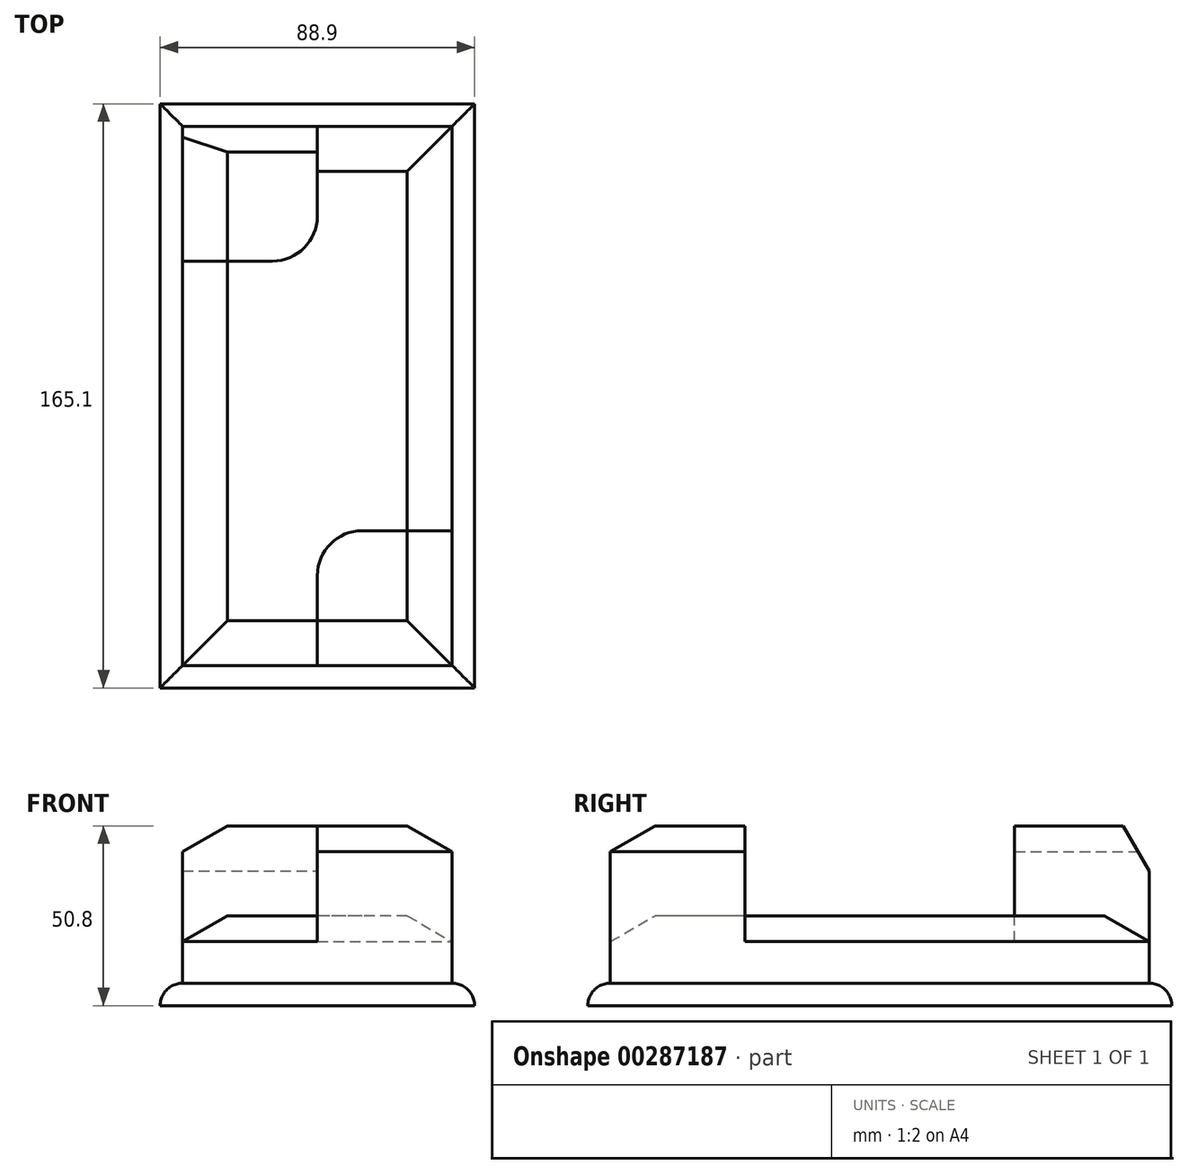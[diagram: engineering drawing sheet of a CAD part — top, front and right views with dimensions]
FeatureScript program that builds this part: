
annotation { "Feature Type Name" : "Feature", "Feature Type Description" : "" }
export const myFeature = defineFeature(function(context is Context, id is Id, definition is map)
    precondition{}
    {
        {
            var Q0;
            Q0=qCreatedBy(makeId("Top.planeOp"),FACE);
            var sketch = newSketch(context, id + "F0", { "sketchPlane" : qUnion([Q0])});
            skLineSegment(sketch, "E0.bottom", {"start": v(-49.01, 97.54) * mm, "end": v(27.19, 97.54) * mm});
            skLineSegment(sketch, "E0.top", {"start": v(-49.01, -54.86) * mm, "end": v(27.19, -54.86) * mm});
            skLineSegment(sketch, "E0.left", {"start": v(-49.01, 97.54) * mm, "end": v(-49.01, -54.86) * mm});
            skLineSegment(sketch, "E0.right", {"start": v(27.19, 97.54) * mm, "end": v(27.19, -54.86) * mm});
            skLineSegment(sketch, "E1.0", {"start": v(-55.36, 103.89) * mm, "end": v(-55.36, -61.21) * mm});
            skLineSegment(sketch, "E1.1", {"start": v(-55.36, 103.89) * mm, "end": v(33.54, 103.89) * mm});
            skLineSegment(sketch, "E1.2", {"start": v(33.54, 103.89) * mm, "end": v(33.54, -61.21) * mm});
            skLineSegment(sketch, "E1.3", {"start": v(-55.36, -61.21) * mm, "end": v(33.54, -61.21) * mm});
            skLineSegment(sketch, "E2", {"start": v(-10.91, 97.54) * mm, "end": v(-10.91, 72.14) * mm});
            skLineSegment(sketch, "E3", {"start": v(-23.61, 59.44) * mm, "end": v(-49.01, 59.44) * mm});
            skLineSegment(sketch, "E4", {"start": v(-10.91, -54.86) * mm, "end": v(-10.91, -29.46) * mm});
            skLineSegment(sketch, "E5", {"start": v(1.79, -16.76) * mm, "end": v(27.19, -16.76) * mm});
            skPoint(sketch, "E6.visualSharp", {"position": v(-10.91, 59.44) * mm});
            skArc(sketch, "E6.filletArc", {"start": v(-23.61, 59.44) * mm, "mid": v(-14.63, 63.16) * mm, "end": v(-10.91, 72.14) * mm});
            skPoint(sketch, "E7.visualSharp", {"position": v(-10.91, -16.76) * mm});
            skArc(sketch, "E7.filletArc", {"start": v(1.79, -16.76) * mm, "mid": v(-7.2, -20.48) * mm, "end": v(-10.91, -29.46) * mm});
            skSolve(sketch);
        }
        {
            var Q0;
            Q0 = qSketchRegion(id + "F0", true);
            var Q1;
            {var subQ9=sQuery(id+"F0.wireOp",EDGE,"E2");Q1=makeQuery(id+"F0.imprint","IMPRINT",FACE,{"disambiguationData":[TD([[makeQuery(id+"F0.imprint","IMPRINT",EDGE,{"derivedFrom":subQ9}),1.0]])]});}
            var Q2;
            {var subQ1=sQuery(id+"F0.wireOp",EDGE,"E2");Q2=makeQuery(id+"F0.imprint","IMPRINT",FACE,{"disambiguationData":[TD([[makeQuery(id+"F0.imprint","IMPRINT",EDGE,{"derivedFrom":subQ1}),-1.0]])]});}
            var Q3;
            {var subQ1=sQuery(id+"F0.wireOp",EDGE,"E4");Q3=makeQuery(id+"F0.imprint","IMPRINT",FACE,{"disambiguationData":[TD([[makeQuery(id+"F0.imprint","IMPRINT",EDGE,{"derivedFrom":subQ1}),-1.0]])]});}
            extrude(context, id + "F1", {"entities" : qUnion([Q0, Q1, Q2, Q3]), "depth" : 6.35 * mm});
        }
        {
            var Q0;
            Q0=makeQuery(id+"F1.opExtrude","CAP_FACE",FACE,{"disambiguationData":[OSD([sQuery(id+"F0.wireOp",EDGE,"E1.0"),sQuery(id+"F0.wireOp",EDGE,"E1.1"),sQuery(id+"F0.wireOp",EDGE,"E1.2"),sQuery(id+"F0.wireOp",EDGE,"E1.3")])],"isStart":false});
            fillet(context, id + "F2", {"entities" : qUnion([Q0]), "radius" : 6.35 * mm, "tangentPropagation" : true, "allowEdgeOverflow" : false});
        }
        {
            var Q0;
            Q0=makeQuery(id+"F1.opExtrude","CAP_FACE",FACE,{"disambiguationData":[OSD([sQuery(id+"F0.wireOp",EDGE,"E1.0"),sQuery(id+"F0.wireOp",EDGE,"E1.1"),sQuery(id+"F0.wireOp",EDGE,"E1.2"),sQuery(id+"F0.wireOp",EDGE,"E1.3")])],"isStart":false});
            extrude(context, id + "F3", {"entities" : qUnion([Q0]), "operationType" : NewBodyOperationType.ADD, "depth" : 19.05 * mm});
        }
        {
            var Q0;
            {var subQ0=sQuery(id+"F0.wireOp",EDGE,"E1.3");var subQ1=sQuery(id+"F0.wireOp",EDGE,"E1.2");var subQ2=sQuery(id+"F0.wireOp",EDGE,"E1.1");var subQ3=sQuery(id+"F0.wireOp",EDGE,"E1.0");Q0=makeQuery(id+"F3.opExtrude","CAP_EDGE",EDGE,{"disambiguationData":[OSD([subQ3,subQ2,subQ1,subQ0]),TDD([makeQuery(id+"F2.opFillet","BLEND_EDGE",EDGE,{"blendedFrom":[makeQuery(id+"F1.opExtrude","CAP_EDGE",EDGE,{"disambiguationData":[OSD([subQ3])],"isStart":false}),makeQuery(id+"F1.opExtrude","CAP_FACE",FACE,{"disambiguationData":[OSD([subQ3,subQ2,subQ1,subQ0])],"isStart":false})],"blendedInto":[makeQuery(id+"F1.opExtrude","CAP_FACE",FACE,{"disambiguationData":[OSD([subQ3,subQ2,subQ1,subQ0])],"isStart":false})]})])],"isStart":false});}
            var Q1;
            Q1=makeQuery(id+"F3.opExtrude","CAP_FACE",FACE,{"disambiguationData":[OSD([sQuery(id+"F0.wireOp",EDGE,"E1.0"),sQuery(id+"F0.wireOp",EDGE,"E1.1"),sQuery(id+"F0.wireOp",EDGE,"E1.2"),sQuery(id+"F0.wireOp",EDGE,"E1.3")])],"isStart":false});
            chamfer(context, id + "F4", {"entities" : qUnion([Q0, Q1]), "chamferType" : ChamferType.OFFSET_ANGLE, "width" : 12.7 * mm, "oppositeDirection" : false, "angle" : 30 * degree, "tangentPropagation" : true});
        }
        {
            var Q0;
            {var subQ1=sQuery(id+"F0.wireOp",EDGE,"E2");Q0=makeQuery(id+"F0.imprint","IMPRINT",FACE,{"disambiguationData":[TD([[makeQuery(id+"F0.imprint","IMPRINT",EDGE,{"derivedFrom":subQ1}),-1.0]])]});}
            var Q1;
            {var subQ1=sQuery(id+"F0.wireOp",EDGE,"E4");Q1=makeQuery(id+"F0.imprint","IMPRINT",FACE,{"disambiguationData":[TD([[makeQuery(id+"F0.imprint","IMPRINT",EDGE,{"derivedFrom":subQ1}),-1.0]])]});}
            extrude(context, id + "F5", {"entities" : qUnion([Q0, Q1]), "operationType" : NewBodyOperationType.ADD, "depth" : 50.8 * mm});
        }
        {
            var Q0;
            Q0=makeQuery(id+"F5.opExtrude","CAP_EDGE",EDGE,{"disambiguationData":[OSD([sQuery(id+"F0.wireOp",EDGE,"E0.top")])],"isStart":false});
            var Q1;
            Q1=makeQuery(id+"F5.opExtrude","CAP_EDGE",EDGE,{"disambiguationData":[OSD([sQuery(id+"F0.wireOp",EDGE,"E0.right")])],"isStart":false});
            var Q2;
            Q2=makeQuery(id+"F5.opExtrude","CAP_EDGE",EDGE,{"disambiguationData":[OSD([sQuery(id+"F0.wireOp",EDGE,"E0.bottom")])],"isStart":false});
            var Q3;
            Q3=makeQuery(id+"F5.opExtrude","CAP_EDGE",EDGE,{"disambiguationData":[OSD([sQuery(id+"F0.wireOp",EDGE,"E0.left")])],"isStart":false});
            chamfer(context, id + "F6", {"entities" : qUnion([Q0, Q1, Q2, Q3]), "chamferType" : ChamferType.OFFSET_ANGLE, "width" : 12.7 * mm, "oppositeDirection" : false, "angle" : 30 * degree, "tangentPropagation" : true});
        }
    });
